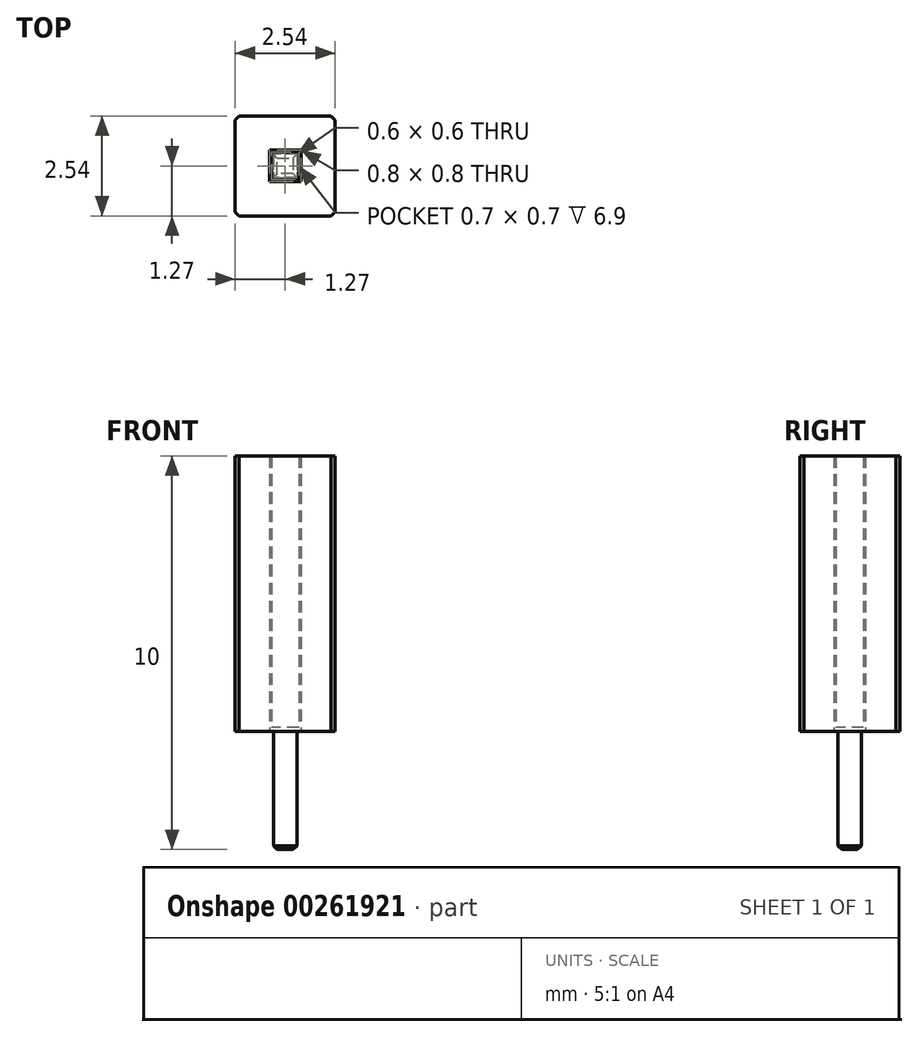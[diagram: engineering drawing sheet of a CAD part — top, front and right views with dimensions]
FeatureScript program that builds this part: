
annotation { "Feature Type Name" : "Feature", "Feature Type Description" : "" }
export const myFeature = defineFeature(function(context is Context, id is Id, definition is map)
    precondition{}
    {
        {
            var Q0;
            Q0=qCreatedBy(makeId("Top.planeOp"),FACE);
            var sketch = newSketch(context, id + "F0", { "sketchPlane" : qUnion([Q0])});
            skLineSegment(sketch, "E0.bottom", {"start": v(1.27, 1.27) * mm, "end": v(-1.27, 1.27) * mm});
            skLineSegment(sketch, "E0.top", {"start": v(1.27, -1.27) * mm, "end": v(-1.27, -1.27) * mm});
            skLineSegment(sketch, "E0.left", {"start": v(1.27, 1.27) * mm, "end": v(1.27, -1.27) * mm});
            skLineSegment(sketch, "E0.right", {"start": v(-1.27, 1.27) * mm, "end": v(-1.27, -1.27) * mm});
            skPoint(sketch, "E0.middle", {"position": v(0, 0) * mm});
            skLineSegment(sketch, "E1.bottom", {"start": v(0.4, 0.4) * mm, "end": v(-0.4, 0.4) * mm});
            skLineSegment(sketch, "E1.top", {"start": v(0.4, -0.4) * mm, "end": v(-0.4, -0.4) * mm});
            skLineSegment(sketch, "E1.left", {"start": v(0.4, 0.4) * mm, "end": v(0.4, -0.4) * mm});
            skLineSegment(sketch, "E1.right", {"start": v(-0.4, 0.4) * mm, "end": v(-0.4, -0.4) * mm});
            skSolve(sketch);
        }
        {
            var Q0;
            Q0 = qSketchRegion(id + "F0", true);
            extrude(context, id + "F1", {"entities" : qUnion([Q0]), "depth" : 7 * mm});
        }
        {
            var Q0;
            Q0=makeQuery(id+"F1.opExtrude","SWEPT_EDGE",EDGE,{"disambiguationData":[OSD([sQuery(id+"F0.wireOp",EDGE,"E0.top"),sQuery(id+"F0.wireOp",EDGE,"E0.left")])]});
            var Q1;
            Q1=makeQuery(id+"F1.opExtrude","SWEPT_EDGE",EDGE,{"disambiguationData":[OSD([sQuery(id+"F0.wireOp",EDGE,"E0.top"),sQuery(id+"F0.wireOp",EDGE,"E0.right")])]});
            var Q2;
            Q2=makeQuery(id+"F1.opExtrude","SWEPT_EDGE",EDGE,{"disambiguationData":[OSD([sQuery(id+"F0.wireOp",EDGE,"E0.bottom"),sQuery(id+"F0.wireOp",EDGE,"E0.right")])]});
            var Q3;
            Q3=makeQuery(id+"F1.opExtrude","SWEPT_EDGE",EDGE,{"disambiguationData":[OSD([sQuery(id+"F0.wireOp",EDGE,"E0.bottom"),sQuery(id+"F0.wireOp",EDGE,"E0.left")])]});
            chamfer(context, id + "F2", {"entities" : qUnion([Q0, Q1, Q2, Q3]), "width" : 0.1 * mm, "tangentPropagation" : true});
        }
        {
            var Q0;
            Q0=qCreatedBy(makeId("Top.planeOp"),FACE);
            var sketch = newSketch(context, id + "F3", { "sketchPlane" : qUnion([Q0])});
            skLineSegment(sketch, "E2.bottom", {"start": v(0.3, 0.3) * mm, "end": v(-0.3, 0.3) * mm});
            skLineSegment(sketch, "E2.top", {"start": v(0.3, -0.3) * mm, "end": v(-0.3, -0.3) * mm});
            skLineSegment(sketch, "E2.left", {"start": v(0.3, 0.3) * mm, "end": v(0.3, -0.3) * mm});
            skLineSegment(sketch, "E2.right", {"start": v(-0.3, 0.3) * mm, "end": v(-0.3, -0.3) * mm});
            skPoint(sketch, "E2.middle", {"position": v(0, 0) * mm});
            skLineSegment(sketch, "E3.bottom", {"start": v(0.35, 0.35) * mm, "end": v(-0.35, 0.35) * mm});
            skLineSegment(sketch, "E3.top", {"start": v(0.35, -0.35) * mm, "end": v(-0.35, -0.35) * mm});
            skLineSegment(sketch, "E3.left", {"start": v(0.35, 0.35) * mm, "end": v(0.35, -0.35) * mm});
            skLineSegment(sketch, "E3.right", {"start": v(-0.35, 0.35) * mm, "end": v(-0.35, -0.35) * mm});
            skLineSegment(sketch, "E4.0", {"start": v(0.4, 0.4) * mm, "end": v(-0.4, 0.4) * mm});
            skLineSegment(sketch, "E4.1", {"start": v(-0.4, 0.4) * mm, "end": v(-0.4, -0.4) * mm});
            skLineSegment(sketch, "E4.2", {"start": v(0.4, 0.4) * mm, "end": v(0.4, -0.4) * mm});
            skLineSegment(sketch, "E4.3", {"start": v(0.4, -0.4) * mm, "end": v(-0.4, -0.4) * mm});
            skSolve(sketch);
        }
        {
            var Q0;
            Q0=makeQuery(id+"F3.imprint","IMPRINT",FACE,{"disambiguationData":[TD([[makeQuery(id+"F3.imprint","IMPRINT",EDGE,{"derivedFrom":sQuery(id+"F3.wireOp",EDGE,"E3.bottom")}),-1.0]])]});
            var Q1;
            Q1=makeQuery(id+"F1.opExtrude","CAP_FACE",FACE,{"disambiguationData":[OSD([sQuery(id+"F0.wireOp",EDGE,"E0.bottom"),sQuery(id+"F0.wireOp",EDGE,"E0.top"),sQuery(id+"F0.wireOp",EDGE,"E0.left"),sQuery(id+"F0.wireOp",EDGE,"E0.right"),sQuery(id+"F0.wireOp",EDGE,"E1.bottom"),sQuery(id+"F0.wireOp",EDGE,"E1.top"),sQuery(id+"F0.wireOp",EDGE,"E1.left"),sQuery(id+"F0.wireOp",EDGE,"E1.right")])],"isStart":false});
            extrude(context, id + "F4", {"entities" : qUnion([Q0]), "endBound" : BoundingType.UP_TO_SURFACE, "endBoundEntityFace" : qUnion([Q1]), "depth" : 25 * mm});
        }
        {
            var Q0;
            Q0=makeQuery(id+"F3.imprint","IMPRINT",FACE,{"disambiguationData":[TD([[makeQuery(id+"F3.imprint","IMPRINT",EDGE,{"derivedFrom":sQuery(id+"F3.wireOp",EDGE,"E2.bottom")}),-1.0]])]});
            extrude(context, id + "F5", {"entities" : qUnion([Q0]), "operationType" : NewBodyOperationType.ADD, "depth" : 0.1 * mm});
        }
        {
            var Q0;
            Q0=makeQuery(id+"F3.imprint","IMPRINT",FACE,{"disambiguationData":[TD([[makeQuery(id+"F3.imprint","IMPRINT",EDGE,{"derivedFrom":sQuery(id+"F3.wireOp",EDGE,"E2.bottom")}),1.0]])]});
            extrude(context, id + "F6", {"entities" : qUnion([Q0]), "operationType" : NewBodyOperationType.ADD, "oppositeDirection" : true, "depth" : 3 * mm, "hasSecondDirection" : true, "secondDirectionOppositeDirection" : false, "secondDirectionDepth" : 0.1 * mm});
        }
        {
            var Q0;
            Q0=makeQuery(id+"F6.opExtrude","CAP_FACE",FACE,{"disambiguationData":[OSD([sQuery(id+"F3.wireOp",EDGE,"E2.bottom"),sQuery(id+"F3.wireOp",EDGE,"E2.top"),sQuery(id+"F3.wireOp",EDGE,"E2.left"),sQuery(id+"F3.wireOp",EDGE,"E2.right")])],"isStart":false});
            chamfer(context, id + "F7", {"entities" : qUnion([Q0]), "width" : 0.1 * mm, "tangentPropagation" : true});
        }
    });
